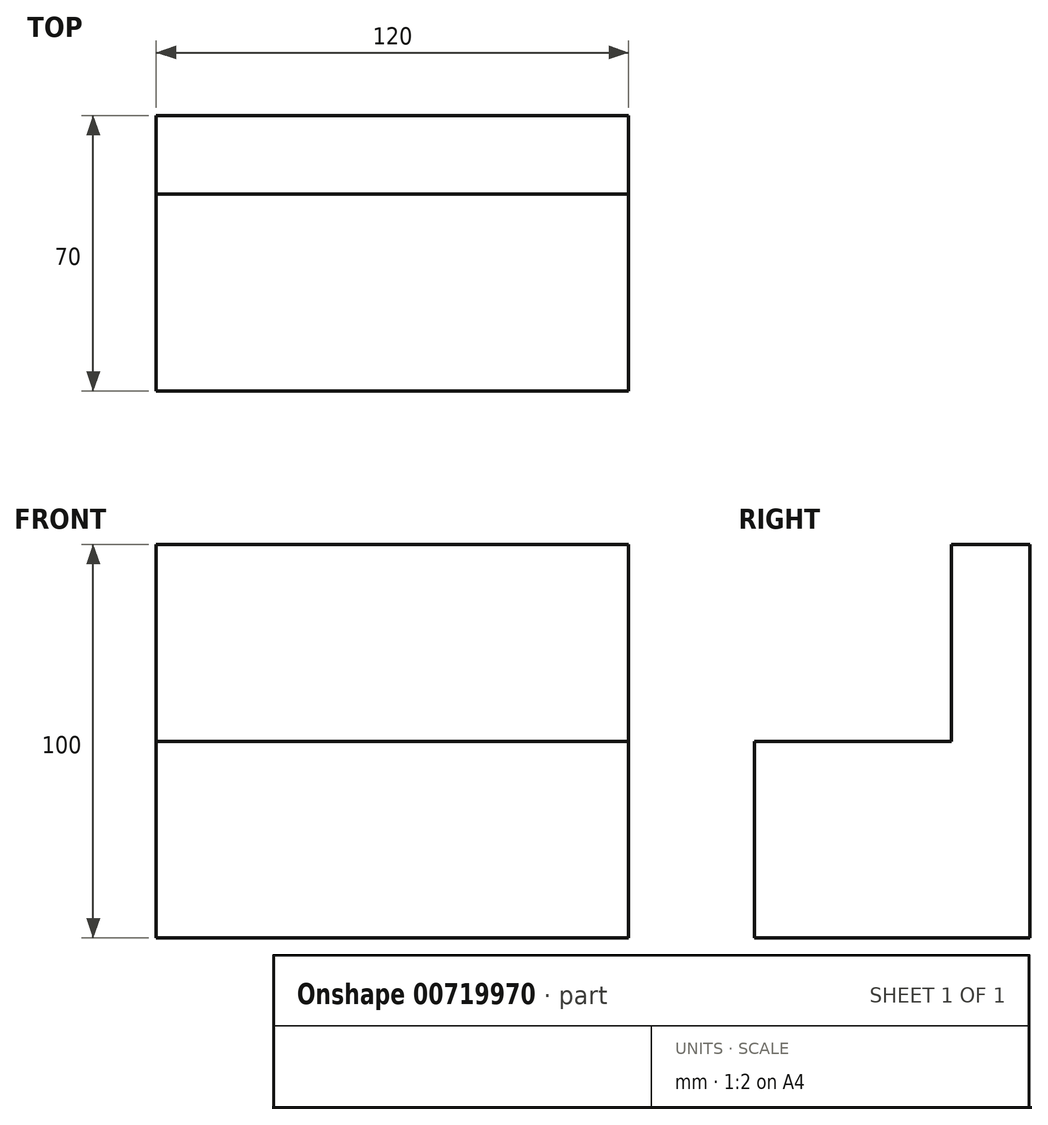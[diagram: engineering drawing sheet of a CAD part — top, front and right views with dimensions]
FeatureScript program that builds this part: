
annotation { "Feature Type Name" : "Feature", "Feature Type Description" : "" }
export const myFeature = defineFeature(function(context is Context, id is Id, definition is map)
    precondition{}
    {
        {
            var Q0;
            Q0=qCreatedBy(makeId("Top.planeOp"),FACE);
            var sketch = newSketch(context, id + "F0", { "sketchPlane" : qUnion([Q0])});
            skLineSegment(sketch, "E0.bottom", {"start": v(-107.85, 32.78) * mm, "end": v(12.15, 32.78) * mm});
            skLineSegment(sketch, "E0.top", {"start": v(-107.85, -37.22) * mm, "end": v(12.15, -37.22) * mm});
            skLineSegment(sketch, "E0.left", {"start": v(-107.85, 32.78) * mm, "end": v(-107.85, -37.22) * mm});
            skLineSegment(sketch, "E0.right", {"start": v(12.15, 32.78) * mm, "end": v(12.15, -37.22) * mm});
            skSolve(sketch);
        }
        {
            var Q0;
            Q0=makeQuery(id+"F0.imprint","IMPRINT",FACE,{"disambiguationData":[TD([[makeQuery(id+"F0.imprint","IMPRINT",EDGE,{"derivedFrom":sQuery(id+"F0.wireOp",EDGE,"E0.bottom")}),-1.0]])]});
            extrude(context, id + "F1", {"entities" : qUnion([Q0]), "depth" : 50 * mm, "offsetDistance" : 25 * mm});
        }
        {
            var Q0;
            Q0=makeQuery(id+"F1.opExtrude","CAP_FACE",FACE,{"disambiguationData":[OSD([sQuery(id+"F0.wireOp",EDGE,"E0.bottom"),sQuery(id+"F0.wireOp",EDGE,"E0.top"),sQuery(id+"F0.wireOp",EDGE,"E0.left"),sQuery(id+"F0.wireOp",EDGE,"E0.right")])],"isStart":false});
            var sketch = newSketch(context, id + "F2", { "sketchPlane" : qUnion([Q0])});
            skLineSegment(sketch, "E1", {"start": v(-92.85, 12.78) * mm, "end": v(77.15, 12.78) * mm});
            skLineSegment(sketch, "E2", {"start": v(12.15, 12.78) * mm, "end": v(77.15, 12.78) * mm});
            skLineSegment(sketch, "E3", {"start": v(12.15, 12.78) * mm, "end": v(-107.85, 12.78) * mm});
            skSolve(sketch);
        }
        {
            var Q0;
            {var subQ1=makeQuery(id+"F1.opExtrude","CAP_EDGE",EDGE,{"disambiguationData":[OSD([sQuery(id+"F0.wireOp",EDGE,"E0.bottom")])],"isStart":false});Q0=makeQuery(id+"F2.imprint","IMPRINT",FACE,{"disambiguationData":[TD([[makeQuery(id+"F2.imprint","IMPRINT",EDGE,{"derivedFrom":subQ1}),-1.0]])]});}
            extrude(context, id + "F3", {"entities" : qUnion([Q0]), "operationType" : NewBodyOperationType.ADD, "depth" : 50 * mm, "offsetDistance" : 25 * mm});
        }
    });
